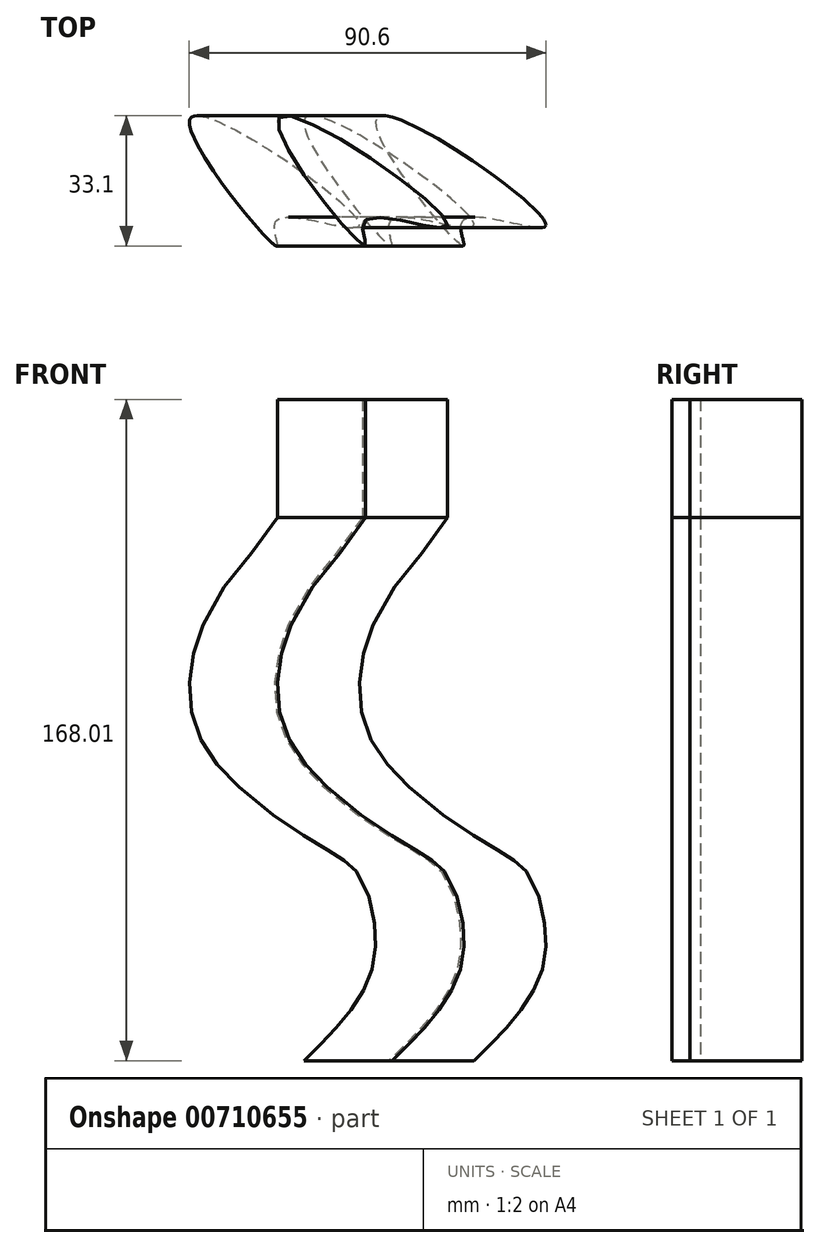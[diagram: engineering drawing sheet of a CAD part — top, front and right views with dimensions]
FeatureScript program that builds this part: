
annotation { "Feature Type Name" : "Feature", "Feature Type Description" : "" }
export const myFeature = defineFeature(function(context is Context, id is Id, definition is map)
    precondition{}
    {
        {
            var Q0;
            Q0=qCreatedBy(makeId("Top.planeOp"),FACE);
            var sketch = newSketch(context, id + "F0", { "sketchPlane" : qUnion([Q0])});
            skFitSpline(sketch, "E0", {"points": [v(0, 0) * mm, v(0, 6.5) * mm, v(20.99, 5.25) * mm, v(-21.81, 32.6) * mm, v(0, 0) * mm]});
            skSolve(sketch);
        }
        {
            var Q0;
            Q0=qCreatedBy(makeId("Front.planeOp"),FACE);
            var sketch = newSketch(context, id + "F1", { "sketchPlane" : qUnion([Q0])});
            skFitSpline(sketch, "E1", {"points": [v(0, 0) * mm, v(18.22, 28.35) * mm, v(14.65, 46.19) * mm, v(6.56, 53.14) * mm, v(-26.51, 82.4) * mm, v(-23.53, 115.14) * mm, v(-6.68, 138) * mm], "startDerivative": vector(209.08, 198.53) * mm, "endDerivative": vector(136.53, 203.6) * mm});
            skSolve(sketch);
        }
        {
            var Q0;
            Q0=makeQuery(id+"F0.imprint","IMPRINT",FACE,{"disambiguationData":[TD([[makeQuery(id+"F0.imprint","IMPRINT",EDGE,{"derivedFrom":sQuery(id+"F0.wireOp",EDGE,"E0")}),1.0]])]});
            var Q1;
            Q1=sQuery(id+"F1.wireOp",EDGE,"E1");
            sweep(context, id + "F2", {"profiles" : qUnion([Q0]), "path" : qUnion([Q1]), "keepProfileOrientation" : true});
        }
        {
            var Q0;
            Q0=makeQuery(id+"F2.opSweep","CAP_FACE",FACE,{"disambiguationData":[OSD([sQuery(id+"F0.wireOp",EDGE,"E0"),sQuery(id+"F1.wireOp",VERTEX,"E1.end")])],"isStart":false});
            extrude(context, id + "F3", {"entities" : qUnion([Q0]), "operationType" : NewBodyOperationType.ADD, "depth" : 30 * mm, "offsetDistance" : 25 * mm});
        }
    });
